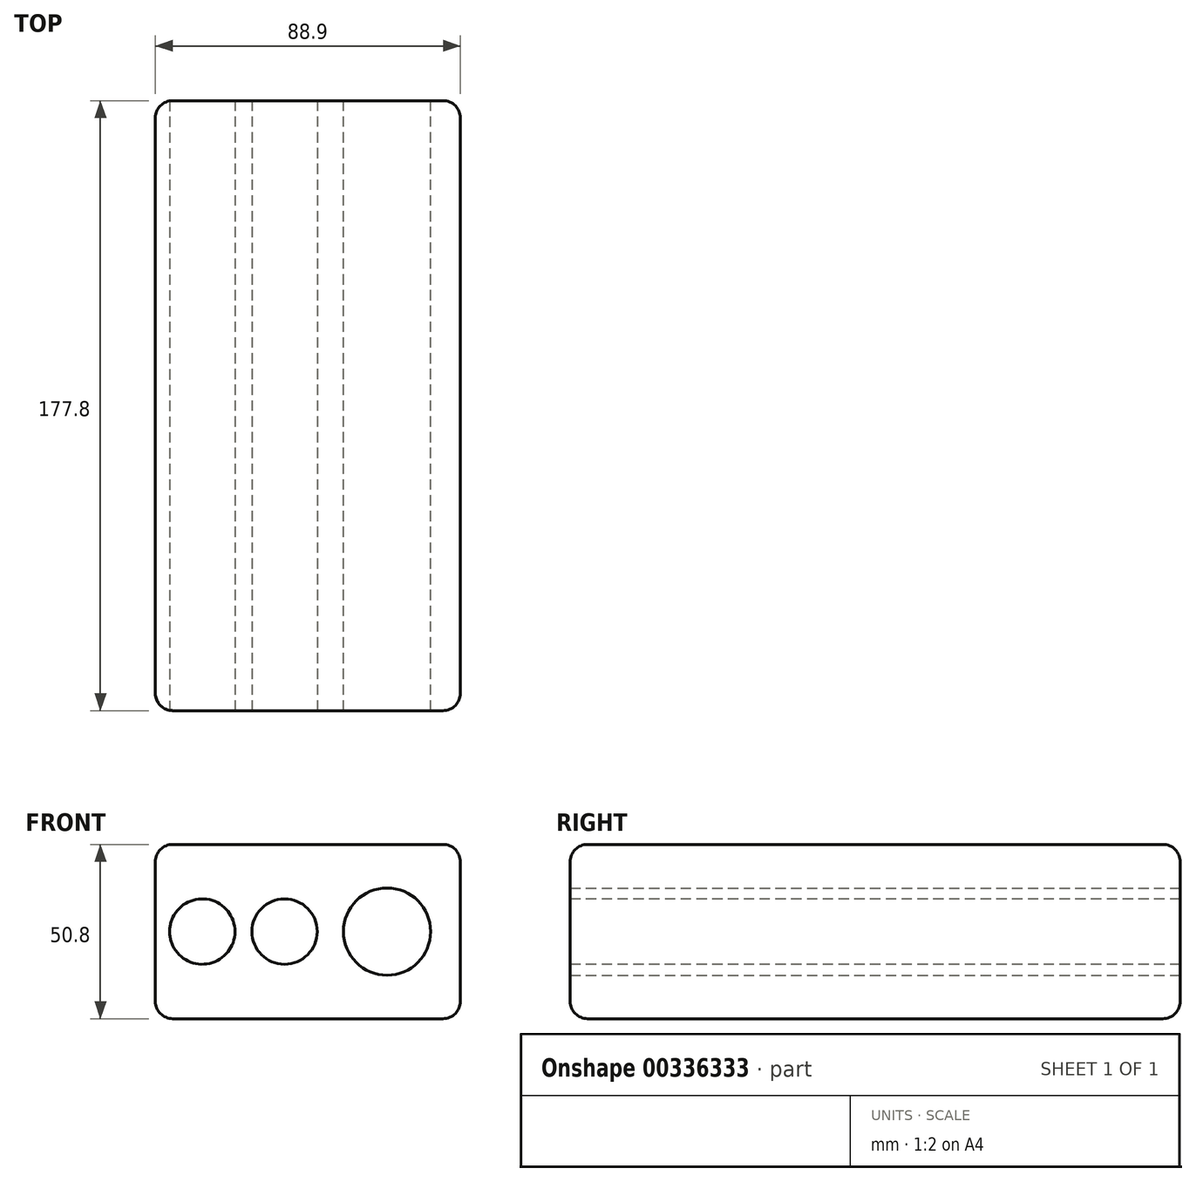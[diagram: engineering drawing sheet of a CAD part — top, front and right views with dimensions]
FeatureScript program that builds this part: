
annotation { "Feature Type Name" : "Feature", "Feature Type Description" : "" }
export const myFeature = defineFeature(function(context is Context, id is Id, definition is map)
    precondition{}
    {
        {
            var Q0;
            Q0=qCreatedBy(makeId("Front.planeOp"),FACE);
            var sketch = newSketch(context, id + "F0", { "sketchPlane" : qUnion([Q0])});
            skLineSegment(sketch, "E0.bottom", {"start": v(44.45, -25.4) * mm, "end": v(-44.45, -25.4) * mm});
            skLineSegment(sketch, "E0.top", {"start": v(44.45, 25.4) * mm, "end": v(-44.45, 25.4) * mm});
            skLineSegment(sketch, "E0.left", {"start": v(44.45, -25.4) * mm, "end": v(44.45, 25.4) * mm});
            skLineSegment(sketch, "E0.right", {"start": v(-44.45, -25.4) * mm, "end": v(-44.45, 25.4) * mm});
            skPoint(sketch, "E0.middle", {"position": v(0, 0) * mm});
            skSolve(sketch);
        }
        {
            var Q0;
            Q0=makeQuery(id+"F0.imprint","IMPRINT",FACE,{"disambiguationData":[TD([[makeQuery(id+"F0.imprint","IMPRINT",EDGE,{"derivedFrom":sQuery(id+"F0.wireOp",EDGE,"E0.bottom")}),-1.0]])]});
            extrude(context, id + "F1", {"entities" : qUnion([Q0]), "depth" : 177.8 * mm});
        }
        {
            var Q0;
            Q0=makeQuery(id+"F1.opExtrude","CAP_FACE",FACE,{"disambiguationData":[OSD([sQuery(id+"F0.wireOp",EDGE,"E0.bottom"),sQuery(id+"F0.wireOp",EDGE,"E0.top"),sQuery(id+"F0.wireOp",EDGE,"E0.left"),sQuery(id+"F0.wireOp",EDGE,"E0.right")])],"isStart":false});
            var sketch = newSketch(context, id + "F2", { "sketchPlane" : qUnion([Q0])});
            skPoint(sketch, "E1", {"position": v(-30.77, 0) * mm});
            skPoint(sketch, "E2", {"position": v(-6.81, 0) * mm});
            skPoint(sketch, "E3", {"position": v(20.44, 0) * mm});
            skSolve(sketch);
        }
        {
            var Q0;
            Q0=sQuery(id+"F2.wireOp",VERTEX,"E1");
            var Q1;
            Q1=sQuery(id+"F2.wireOp",VERTEX,"E2");
            var Q2;
            Q2=makeQuery(id+"F1.opExtrude","SWEPT_BODY",BODY,{"disambiguationData":[OSD([sQuery(id+"F0.wireOp",EDGE,"E0.bottom"),sQuery(id+"F0.wireOp",EDGE,"E0.top"),sQuery(id+"F0.wireOp",EDGE,"E0.left"),sQuery(id+"F0.wireOp",EDGE,"E0.right")])]});
            hole(context, id + "F3", {"style" : HoleStyle.SIMPLE, "endStyle" : HoleEndStyle.THROUGH, "holeDiameter" : 19.05 * mm, "tappedDepth" : 12.7 * mm, "tapClearance" : 3, "locations" : qUnion([Q0, Q1]), "scope" : qUnion([Q2])});
        }
        {
            var Q0;
            Q0=qCreatedBy(makeId("Front.planeOp"),FACE);
            var sketch = newSketch(context, id + "F4", { "sketchPlane" : qUnion([Q0])});
            skPoint(sketch, "E4", {"position": v(23.08, 0) * mm});
            skSolve(sketch);
        }
        {
            var Q0;
            Q0=sQuery(id+"F4.wireOp",VERTEX,"E4");
            var Q1;
            Q1=makeQuery(id+"F1.opExtrude","SWEPT_BODY",BODY,{"disambiguationData":[OSD([sQuery(id+"F0.wireOp",EDGE,"E0.bottom"),sQuery(id+"F0.wireOp",EDGE,"E0.top"),sQuery(id+"F0.wireOp",EDGE,"E0.left"),sQuery(id+"F0.wireOp",EDGE,"E0.right")])]});
            hole(context, id + "F5", {"style" : HoleStyle.SIMPLE, "endStyle" : HoleEndStyle.THROUGH, "oppositeDirection" : true, "holeDiameter" : 25.4 * mm, "tappedDepth" : 12.7 * mm, "tapClearance" : 3, "locations" : qUnion([Q0]), "scope" : qUnion([Q1])});
        }
        {
            var Q0;
            Q0=makeQuery(id+"F1.opExtrude","SWEPT_FACE",FACE,{"disambiguationData":[OSD([sQuery(id+"F0.wireOp",EDGE,"E0.top")])]});
            var Q1;
            Q1=makeQuery(id+"F1.opExtrude","SWEPT_FACE",FACE,{"disambiguationData":[OSD([sQuery(id+"F0.wireOp",EDGE,"E0.left")])]});
            var Q2;
            Q2=makeQuery(id+"F1.opExtrude","SWEPT_FACE",FACE,{"disambiguationData":[OSD([sQuery(id+"F0.wireOp",EDGE,"E0.right")])]});
            var Q3;
            Q3=makeQuery(id+"F1.opExtrude","SWEPT_FACE",FACE,{"disambiguationData":[OSD([sQuery(id+"F0.wireOp",EDGE,"E0.bottom")])]});
            fillet(context, id + "F6", {"entities" : qUnion([Q0, Q1, Q2, Q3]), "radius" : 5.08 * mm, "tangentPropagation" : true, "allowEdgeOverflow" : false});
        }
    });
